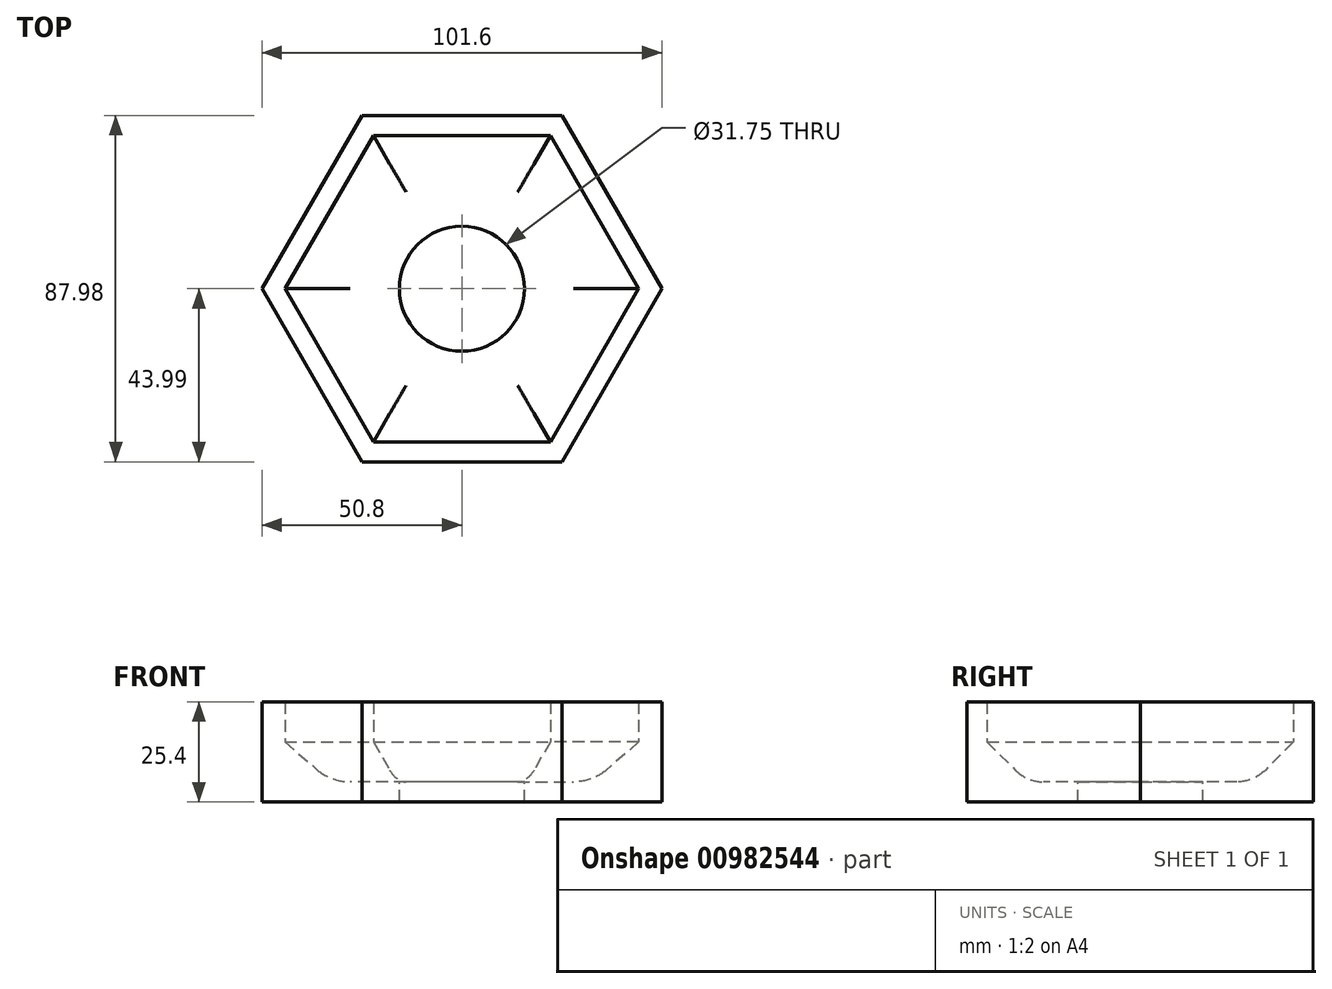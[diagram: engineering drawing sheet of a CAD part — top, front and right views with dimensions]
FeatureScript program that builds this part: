
annotation { "Feature Type Name" : "Feature", "Feature Type Description" : "" }
export const myFeature = defineFeature(function(context is Context, id is Id, definition is map)
    precondition{}
    {
        {
            var Q0;
            Q0=qCreatedBy(makeId("Top.planeOp"),FACE);
            var sketch = newSketch(context, id + "F0", { "sketchPlane" : qUnion([Q0])});
            skCircle(sketch, "E0.cCircle", {"center": v(0, 0) * mm, "radius": 44 * mm, "construction": true});
            skLineSegment(sketch, "E0.0", {"start": v(-25.4, 44) * mm, "end": v(25.4, 44) * mm});
            skLineSegment(sketch, "E0.1", {"start": v(25.4, 44) * mm, "end": v(50.8, 0) * mm});
            skLineSegment(sketch, "E0.2", {"start": v(50.8, 0) * mm, "end": v(25.4, -44) * mm});
            skLineSegment(sketch, "E0.3", {"start": v(25.4, -44) * mm, "end": v(-25.4, -44) * mm});
            skLineSegment(sketch, "E0.4", {"start": v(-25.4, -44) * mm, "end": v(-50.8, 0) * mm});
            skLineSegment(sketch, "E0.5", {"start": v(-50.8, 0) * mm, "end": v(-25.4, 44) * mm});
            skPoint(sketch, "E0.0.midPoint", {"position": v(0, 44) * mm});
            skSolve(sketch);
        }
        {
            var Q0;
            Q0 = qSketchRegion(id + "F0", true);
            extrude(context, id + "F1", {"entities" : qUnion([Q0]), "depth" : 25.4 * mm, "offsetDistance" : 25.4 * mm});
        }
        {
            var Q0;
            Q0=makeQuery(id+"F1.opExtrude","CAP_FACE",FACE,{"disambiguationData":[OSD([sQuery(id+"F0.wireOp",EDGE,"E0.0"),sQuery(id+"F0.wireOp",EDGE,"E0.1"),sQuery(id+"F0.wireOp",EDGE,"E0.2"),sQuery(id+"F0.wireOp",EDGE,"E0.3"),sQuery(id+"F0.wireOp",EDGE,"E0.4"),sQuery(id+"F0.wireOp",EDGE,"E0.5")])],"isStart":false});
            shell(context, id + "F2", {"entities" : qUnion([Q0]), "thickness" : 5.08 * mm});
        }
        {
            var Q0;
            {var subQ0=sQuery(id+"F0.wireOp",EDGE,"E0.0");Q0=makeQuery(id+"F2.opShell","OFFSET_EDGE",EDGE,{"disambiguationData":[OSD([subQ0]),TDD([makeQuery(id+"F1.opExtrude","CAP_EDGE",EDGE,{"disambiguationData":[OSD([subQ0])],"isStart":true})])]});}
            var Q1;
            {var subQ0=sQuery(id+"F0.wireOp",EDGE,"E0.1");Q1=makeQuery(id+"F2.opShell","OFFSET_EDGE",EDGE,{"disambiguationData":[OSD([subQ0]),TDD([makeQuery(id+"F1.opExtrude","CAP_EDGE",EDGE,{"disambiguationData":[OSD([subQ0])],"isStart":true})])]});}
            var Q2;
            {var subQ0=sQuery(id+"F0.wireOp",EDGE,"E0.5");Q2=makeQuery(id+"F2.opShell","OFFSET_EDGE",EDGE,{"disambiguationData":[OSD([subQ0]),TDD([makeQuery(id+"F1.opExtrude","CAP_EDGE",EDGE,{"disambiguationData":[OSD([subQ0])],"isStart":true})])]});}
            var Q3;
            {var subQ0=sQuery(id+"F0.wireOp",EDGE,"E0.4");Q3=makeQuery(id+"F2.opShell","OFFSET_EDGE",EDGE,{"disambiguationData":[OSD([subQ0]),TDD([makeQuery(id+"F1.opExtrude","CAP_EDGE",EDGE,{"disambiguationData":[OSD([subQ0])],"isStart":true})])]});}
            var Q4;
            {var subQ0=sQuery(id+"F0.wireOp",EDGE,"E0.3");Q4=makeQuery(id+"F2.opShell","OFFSET_EDGE",EDGE,{"disambiguationData":[OSD([subQ0]),TDD([makeQuery(id+"F1.opExtrude","CAP_EDGE",EDGE,{"disambiguationData":[OSD([subQ0])],"isStart":true})])]});}
            var Q5;
            {var subQ0=sQuery(id+"F0.wireOp",EDGE,"E0.2");Q5=makeQuery(id+"F2.opShell","OFFSET_EDGE",EDGE,{"disambiguationData":[OSD([subQ0]),TDD([makeQuery(id+"F1.opExtrude","CAP_EDGE",EDGE,{"disambiguationData":[OSD([subQ0])],"isStart":true})])]});}
            chamfer(context, id + "F3", {"entities" : qUnion([Q0, Q1, Q2, Q3, Q4, Q5]), "width" : 10.16 * mm, "tangentPropagation" : true});
        }
        {
            var Q0;
            Q0=makeQuery(id+"F2.opShell","OFFSET_FACE",FACE,{"disambiguationData":[OSD([sQuery(id+"F0.wireOp",EDGE,"E0.0"),sQuery(id+"F0.wireOp",EDGE,"E0.1"),sQuery(id+"F0.wireOp",EDGE,"E0.2"),sQuery(id+"F0.wireOp",EDGE,"E0.3"),sQuery(id+"F0.wireOp",EDGE,"E0.4"),sQuery(id+"F0.wireOp",EDGE,"E0.5")])]});
            fillet(context, id + "F4", {"entities" : qUnion([Q0]), "radius" : 10.16 * mm, "tangentPropagation" : true, "allowEdgeOverflow" : false});
        }
        {
            var Q0;
            Q0=makeQuery(id+"F2.opShell","OFFSET_FACE",FACE,{"disambiguationData":[OSD([sQuery(id+"F0.wireOp",EDGE,"E0.0"),sQuery(id+"F0.wireOp",EDGE,"E0.1"),sQuery(id+"F0.wireOp",EDGE,"E0.2"),sQuery(id+"F0.wireOp",EDGE,"E0.3"),sQuery(id+"F0.wireOp",EDGE,"E0.4"),sQuery(id+"F0.wireOp",EDGE,"E0.5")])]});
            var sketch = newSketch(context, id + "F5", { "sketchPlane" : qUnion([Q0])});
            skCircle(sketch, "E1", {"center": v(0, 0) * mm, "radius": 15.88 * mm});
            skSolve(sketch);
        }
        {
            var Q0;
            Q0=makeQuery(id+"F5.imprint","IMPRINT",FACE,{"disambiguationData":[TD([[makeQuery(id+"F5.imprint","IMPRINT",EDGE,{"derivedFrom":sQuery(id+"F5.wireOp",EDGE,"E1")}),1.0]])]});
            extrude(context, id + "F6", {"entities" : qUnion([Q0]), "operationType" : NewBodyOperationType.REMOVE, "oppositeDirection" : true, "depth" : 25.4 * mm, "offsetDistance" : 25.4 * mm});
        }
    });
